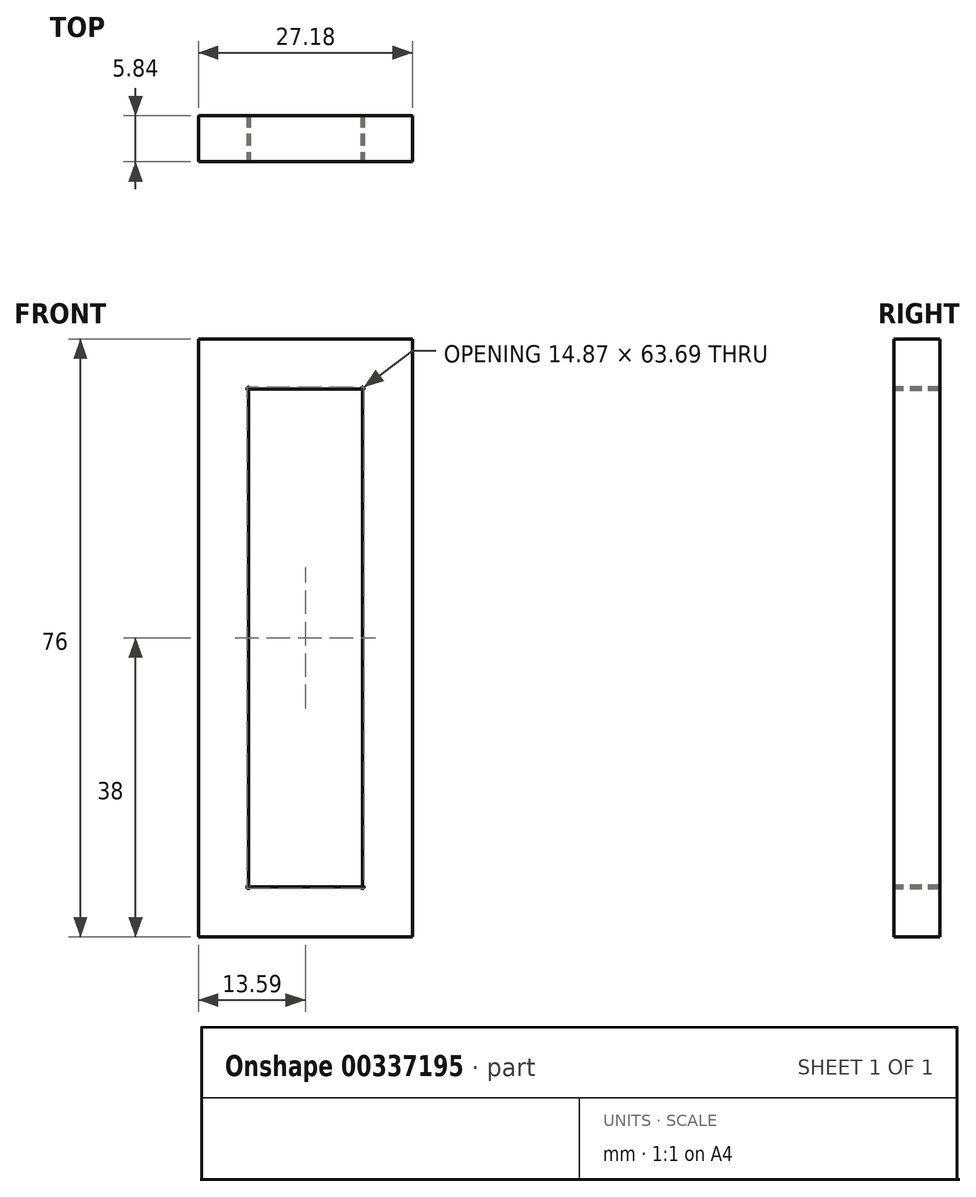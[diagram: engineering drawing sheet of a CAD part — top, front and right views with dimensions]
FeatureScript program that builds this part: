
annotation { "Feature Type Name" : "Feature", "Feature Type Description" : "" }
export const myFeature = defineFeature(function(context is Context, id is Id, definition is map)
    precondition{}
    {
        {
            var Q0;
            Q0=qCreatedBy(makeId("Front.planeOp"),FACE);
            var sketch = newSketch(context, id + "F0", { "sketchPlane" : qUnion([Q0])});
            skLineSegment(sketch, "E0.bottom", {"start": v(-7.24, 31.65) * mm, "end": v(7.24, 31.65) * mm});
            skLineSegment(sketch, "E0.top", {"start": v(-7.24, -31.65) * mm, "end": v(7.24, -31.65) * mm});
            skLineSegment(sketch, "E0.left", {"start": v(-7.24, 31.65) * mm, "end": v(-7.24, -31.65) * mm});
            skLineSegment(sketch, "E0.right", {"start": v(7.24, 31.65) * mm, "end": v(7.24, -31.65) * mm});
            skPoint(sketch, "E0.middle", {"position": v(0, 0) * mm});
            skLineSegment(sketch, "E1.0", {"start": v(13.6, 38) * mm, "end": v(13.6, -38) * mm});
            skLineSegment(sketch, "E1.1", {"start": v(-13.6, 38) * mm, "end": v(13.6, 38) * mm});
            skLineSegment(sketch, "E1.2", {"start": v(-13.6, 38) * mm, "end": v(-13.6, -38) * mm});
            skLineSegment(sketch, "E1.3", {"start": v(-13.6, -38) * mm, "end": v(13.6, -38) * mm});
            skSolve(sketch);
        }
        {
            var Q0;
            Q0=makeQuery(id+"F0.imprint","IMPRINT",FACE,{"disambiguationData":[TD([[makeQuery(id+"F0.imprint","IMPRINT",EDGE,{"derivedFrom":sQuery(id+"F0.wireOp",EDGE,"E0.bottom")}),1.0]])]});
            extrude(context, id + "F1", {"entities" : qUnion([Q0]), "depth" : 5.84 * mm});
        }
        {
            var Q0;
            Q0=makeQuery(id+"F1.opExtrude","CAP_FACE",FACE,{"disambiguationData":[OSD([sQuery(id+"F0.wireOp",EDGE,"E0.bottom"),sQuery(id+"F0.wireOp",EDGE,"E0.top"),sQuery(id+"F0.wireOp",EDGE,"E0.left"),sQuery(id+"F0.wireOp",EDGE,"E0.right"),sQuery(id+"F0.wireOp",EDGE,"E1.0"),sQuery(id+"F0.wireOp",EDGE,"E1.1"),sQuery(id+"F0.wireOp",EDGE,"E1.2"),sQuery(id+"F0.wireOp",EDGE,"E1.3")])],"isStart":false});
            var sketch = newSketch(context, id + "F2", { "sketchPlane" : qUnion([Q0])});
            skCircle(sketch, "E2", {"center": v(-7.24, 31.65) * mm, "radius": 0.2 * mm});
            skLineSegment(sketch, "E3", {"start": v(0, 31.65) * mm, "end": v(0, -31.65) * mm, "construction": true});
            skLineSegment(sketch, "E4", {"start": v(-7.24, 0) * mm, "end": v(7.24, 0) * mm, "construction": true});
            skCircle(sketch, "E5.MirrorC", {"center": v(7.24, 31.65) * mm, "radius": 0.2 * mm});
            skCircle(sketch, "E6.MirrorC", {"center": v(-7.24, -31.65) * mm, "radius": 0.2 * mm});
            skCircle(sketch, "E7.MirrorC", {"center": v(7.24, -31.65) * mm, "radius": 0.2 * mm});
            skSolve(sketch);
        }
        {
            var Q0;
            Q0 = qSketchRegion(id + "F2", true);
            extrude(context, id + "F3", {"entities" : qUnion([Q0]), "operationType" : NewBodyOperationType.REMOVE, "endBound" : BoundingType.THROUGH_ALL, "oppositeDirection" : true, "depth" : 25.4 * mm});
        }
    });
